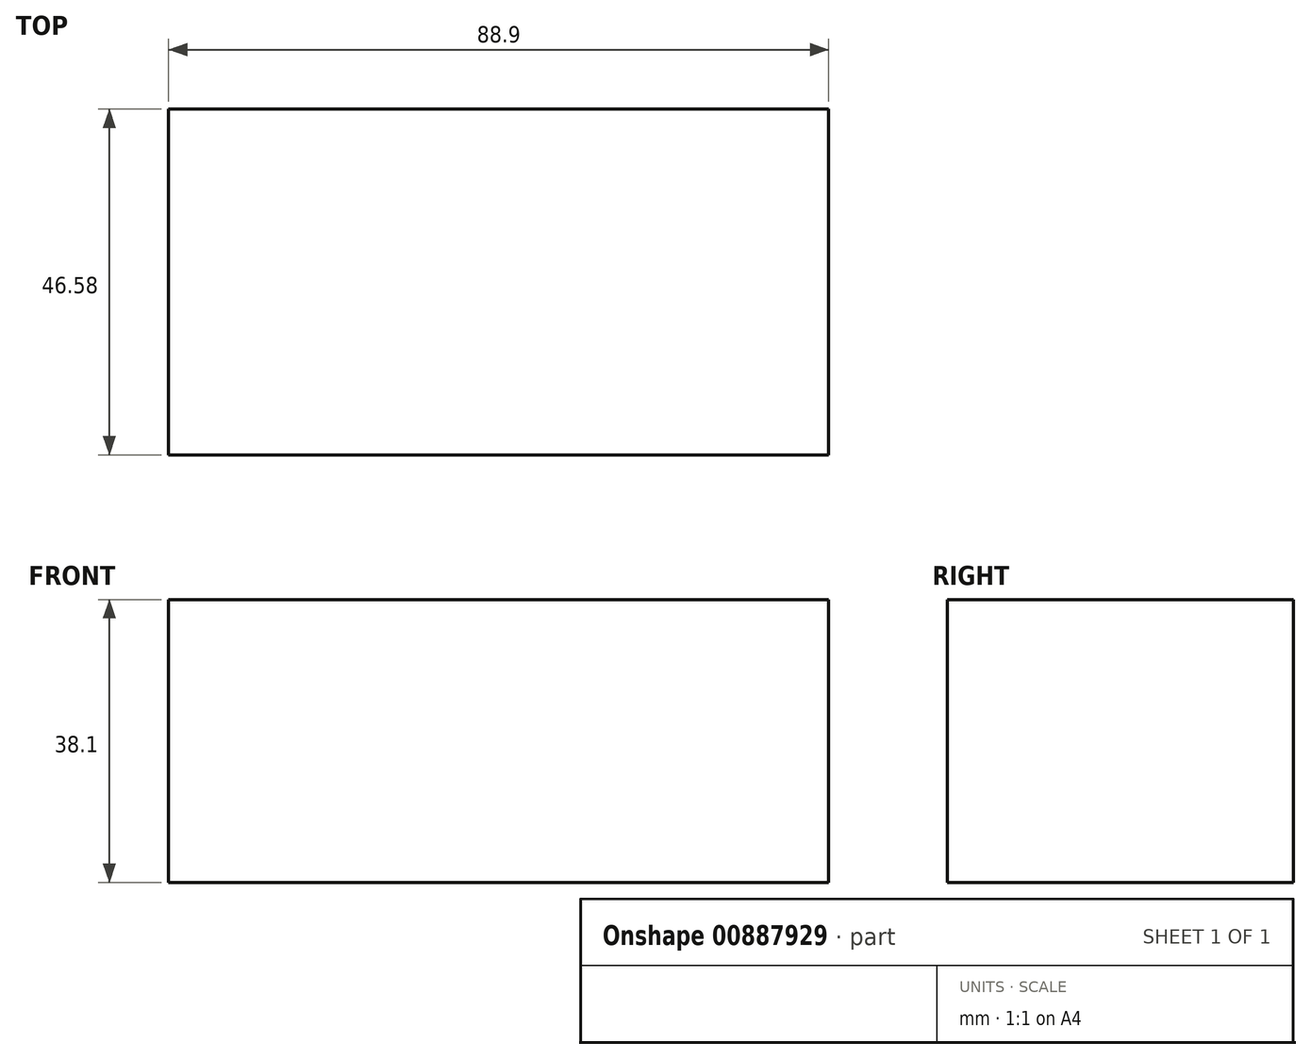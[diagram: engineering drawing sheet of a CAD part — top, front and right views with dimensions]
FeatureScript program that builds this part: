
annotation { "Feature Type Name" : "Feature", "Feature Type Description" : "" }
export const myFeature = defineFeature(function(context is Context, id is Id, definition is map)
    precondition{}
    {
        {
            assignVariable(context, id + "F0", {"name" : "WoodThickness", "anyValue" : .71});
        }
        {
            var Q0;
            Q0=qCreatedBy(makeId("Front.planeOp"),FACE);
            var sketch = newSketch(context, id + "F1", { "sketchPlane" : qUnion([Q0])});
            skLineSegment(sketch, "E0.bottom", {"start": v(44.45, 19.05) * mm, "end": v(-44.45, 19.05) * mm});
            skLineSegment(sketch, "E0.top", {"start": v(44.45, -19.05) * mm, "end": v(-44.45, -19.05) * mm});
            skLineSegment(sketch, "E0.left", {"start": v(44.45, 19.05) * mm, "end": v(44.45, -19.05) * mm});
            skLineSegment(sketch, "E0.right", {"start": v(-44.45, 19.05) * mm, "end": v(-44.45, -19.05) * mm});
            skPoint(sketch, "E0.middle", {"position": v(0, 0) * mm});
            skSolve(sketch);
        }
        {
            var Q0;
            Q0 = qSketchRegion(id + "F1", true);
            extrude(context, id + "F2", {"entities" : qUnion([Q0]), "depth" : (48 - 2 * getVariable(context, 'WoodThickness')) * mm, "offsetDistance" : 25.4 * mm});
        }
    });
